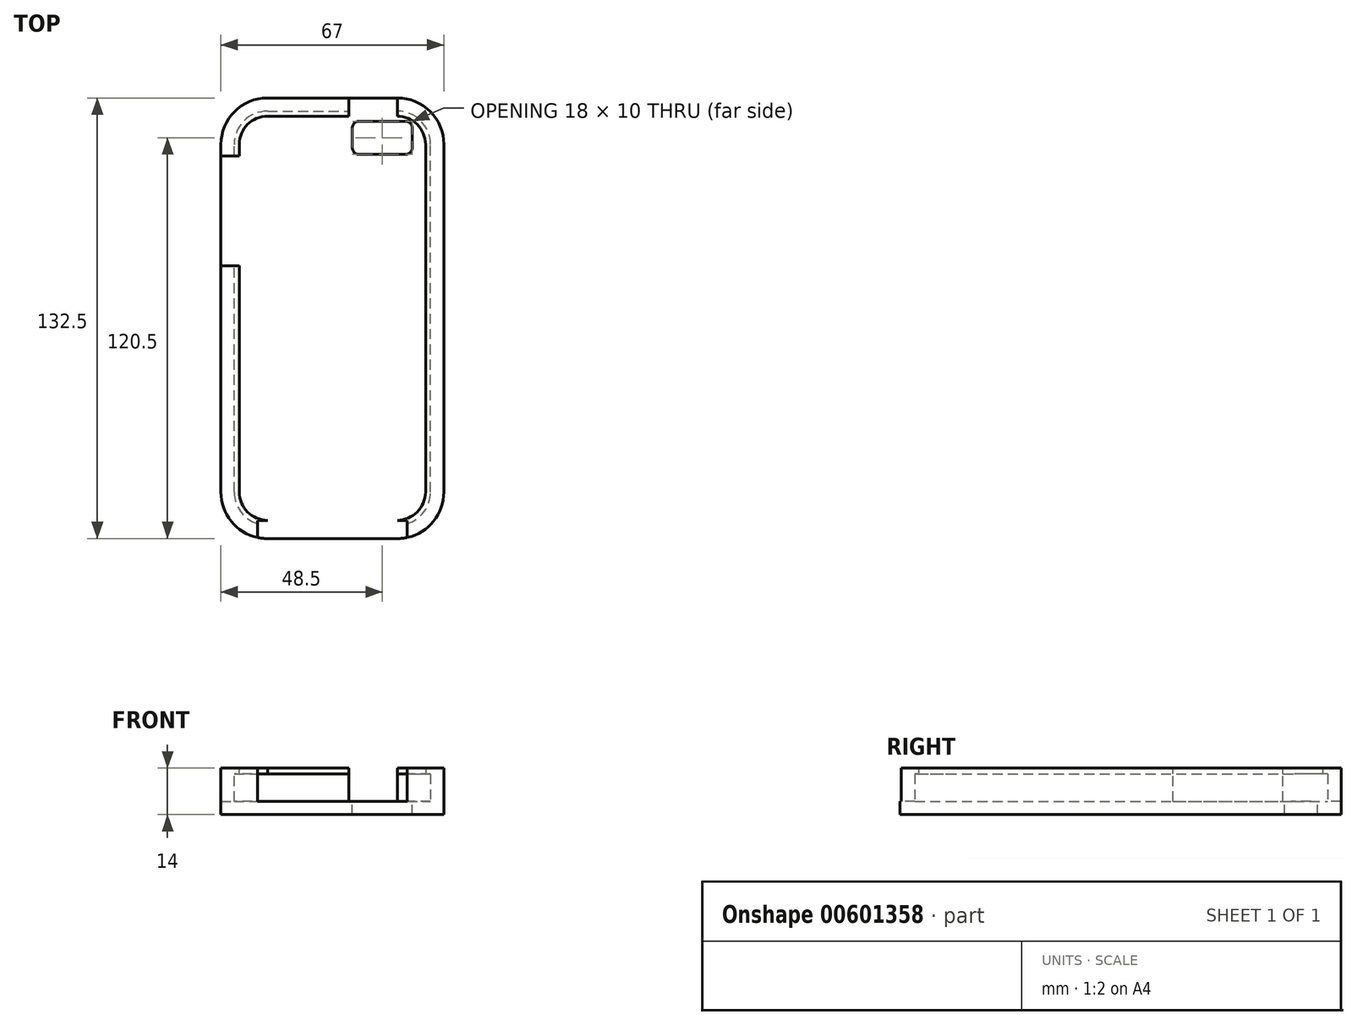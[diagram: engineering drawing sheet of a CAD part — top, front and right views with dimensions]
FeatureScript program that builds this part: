
annotation { "Feature Type Name" : "Feature", "Feature Type Description" : "" }
export const myFeature = defineFeature(function(context is Context, id is Id, definition is map)
    precondition{}
    {
        {
            var Q0;
            Q0=qCreatedBy(makeId("Top.planeOp"),FACE);
            var sketch = newSketch(context, id + "F0", { "sketchPlane" : qUnion([Q0])});
            skLineSegment(sketch, "E0.bottom", {"start": v(10, 0) * mm, "end": v(49, 0) * mm});
            skLineSegment(sketch, "E0.top", {"start": v(10, 124.5) * mm, "end": v(49, 124.5) * mm});
            skLineSegment(sketch, "E0.left", {"start": v(0, 10) * mm, "end": v(0, 114.5) * mm});
            skLineSegment(sketch, "E0.right", {"start": v(59, 10) * mm, "end": v(59, 114.5) * mm});
            skPoint(sketch, "E1.visualSharp", {"position": v(0, 124.5) * mm});
            skArc(sketch, "E1.filletArc", {"start": v(10, 124.5) * mm, "mid": v(2.93, 121.57) * mm, "end": v(0, 114.5) * mm});
            skPoint(sketch, "E2.visualSharp", {"position": v(59, 124.5) * mm});
            skArc(sketch, "E2.filletArc", {"start": v(59, 114.5) * mm, "mid": v(56.07, 121.57) * mm, "end": v(49, 124.5) * mm});
            skPoint(sketch, "E3.visualSharp", {"position": v(59, 0) * mm});
            skArc(sketch, "E3.filletArc", {"start": v(49, 0) * mm, "mid": v(56.07, 2.93) * mm, "end": v(59, 10) * mm});
            skPoint(sketch, "E4.visualSharp", {"position": v(0, 0) * mm});
            skArc(sketch, "E4.filletArc", {"start": v(0, 10) * mm, "mid": v(2.93, 2.93) * mm, "end": v(10, 0) * mm});
            skLineSegment(sketch, "E5.0", {"start": v(63, 10) * mm, "end": v(63, 114.5) * mm});
            skArc(sketch, "E5.1", {"start": v(49, -4) * mm, "mid": v(58.9, 0.1) * mm, "end": v(63, 10) * mm});
            skArc(sketch, "E5.2", {"start": v(63, 114.5) * mm, "mid": v(58.9, 124.4) * mm, "end": v(49, 128.5) * mm});
            skLineSegment(sketch, "E5.3", {"start": v(10, -4) * mm, "end": v(49, -4) * mm});
            skLineSegment(sketch, "E5.4", {"start": v(10, 128.5) * mm, "end": v(49, 128.5) * mm});
            skArc(sketch, "E5.5", {"start": v(10, 128.5) * mm, "mid": v(0.1, 124.4) * mm, "end": v(-4, 114.5) * mm});
            skLineSegment(sketch, "E5.6", {"start": v(-4, 10) * mm, "end": v(-4, 114.5) * mm});
            skArc(sketch, "E5.7", {"start": v(-4, 10) * mm, "mid": v(0.1, 0.1) * mm, "end": v(10, -4) * mm});
            skLineSegment(sketch, "E6.bottom", {"start": v(51.5, 121.5) * mm, "end": v(37.5, 121.5) * mm});
            skLineSegment(sketch, "E6.top", {"start": v(51.5, 111.5) * mm, "end": v(37.5, 111.5) * mm});
            skLineSegment(sketch, "E6.left", {"start": v(53.5, 119.5) * mm, "end": v(53.5, 113.5) * mm});
            skLineSegment(sketch, "E6.right", {"start": v(35.5, 119.5) * mm, "end": v(35.5, 113.5) * mm});
            skPoint(sketch, "E7.visualSharp", {"position": v(35.5, 121.5) * mm});
            skArc(sketch, "E7.filletArc", {"start": v(37.5, 121.5) * mm, "mid": v(36.09, 120.91) * mm, "end": v(35.5, 119.5) * mm});
            skPoint(sketch, "E8.visualSharp", {"position": v(53.5, 121.5) * mm});
            skArc(sketch, "E8.filletArc", {"start": v(53.5, 119.5) * mm, "mid": v(52.91, 120.91) * mm, "end": v(51.5, 121.5) * mm});
            skPoint(sketch, "E9.visualSharp", {"position": v(53.5, 111.5) * mm});
            skArc(sketch, "E9.filletArc", {"start": v(51.5, 111.5) * mm, "mid": v(52.91, 112.09) * mm, "end": v(53.5, 113.5) * mm});
            skPoint(sketch, "E10.visualSharp", {"position": v(35.5, 111.5) * mm});
            skArc(sketch, "E10.filletArc", {"start": v(35.5, 113.5) * mm, "mid": v(36.09, 112.09) * mm, "end": v(37.5, 111.5) * mm});
            skArc(sketch, "E11.0", {"start": v(49, 1.5) * mm, "mid": v(55.01, 3.99) * mm, "end": v(57.5, 10) * mm});
            skLineSegment(sketch, "E11.1", {"start": v(10, 1.5) * mm, "end": v(49, 1.5) * mm});
            skLineSegment(sketch, "E11.2", {"start": v(57.5, 10) * mm, "end": v(57.5, 114.5) * mm});
            skArc(sketch, "E11.3", {"start": v(1.5, 10) * mm, "mid": v(3.99, 3.99) * mm, "end": v(10, 1.5) * mm});
            skArc(sketch, "E11.4", {"start": v(57.5, 114.5) * mm, "mid": v(55.01, 120.51) * mm, "end": v(49, 123) * mm});
            skLineSegment(sketch, "E11.5", {"start": v(10, 123) * mm, "end": v(49, 123) * mm});
            skArc(sketch, "E11.6", {"start": v(10, 123) * mm, "mid": v(3.99, 120.51) * mm, "end": v(1.5, 114.5) * mm});
            skLineSegment(sketch, "E11.7", {"start": v(1.5, 10) * mm, "end": v(1.5, 114.5) * mm});
            skSolve(sketch);
        }
        {
            var Q0;
            Q0=makeQuery(id+"F0.imprint","IMPRINT",FACE,{"disambiguationData":[TD([[makeQuery(id+"F0.imprint","IMPRINT",EDGE,{"derivedFrom":sQuery(id+"F0.wireOp",EDGE,"E6.bottom")}),-1.0]])]});
            var Q1;
            Q1=makeQuery(id+"F0.imprint","IMPRINT",FACE,{"disambiguationData":[TD([[makeQuery(id+"F0.imprint","IMPRINT",EDGE,{"derivedFrom":sQuery(id+"F0.wireOp",EDGE,"E0.bottom")}),-1.0]])]});
            var Q2;
            Q2=makeQuery(id+"F0.imprint","IMPRINT",FACE,{"disambiguationData":[TD([[makeQuery(id+"F0.imprint","IMPRINT",EDGE,{"derivedFrom":sQuery(id+"F0.wireOp",EDGE,"E0.bottom")}),1.0]])]});
            extrude(context, id + "F1", {"entities" : qUnion([Q0, Q1, Q2]), "oppositeDirection" : true, "depth" : 4 * mm, "offsetDistance" : 25 * mm});
        }
        {
            var Q0;
            Q0=makeQuery(id+"F0.imprint","IMPRINT",FACE,{"disambiguationData":[TD([[makeQuery(id+"F0.imprint","IMPRINT",EDGE,{"derivedFrom":sQuery(id+"F0.wireOp",EDGE,"E0.bottom")}),1.0]])]});
            var Q1;
            Q1=makeQuery(id+"F0.imprint","IMPRINT",FACE,{"disambiguationData":[TD([[makeQuery(id+"F0.imprint","IMPRINT",EDGE,{"derivedFrom":sQuery(id+"F0.wireOp",EDGE,"E0.bottom")}),-1.0]])]});
            extrude(context, id + "F2", {"entities" : qUnion([Q0, Q1]), "operationType" : NewBodyOperationType.ADD, "depth" : 10 * mm, "offsetDistance" : 25 * mm});
        }
        {
            var Q0;
            Q0=makeQuery(id+"F0.imprint","IMPRINT",FACE,{"disambiguationData":[TD([[makeQuery(id+"F0.imprint","IMPRINT",EDGE,{"derivedFrom":sQuery(id+"F0.wireOp",EDGE,"E0.bottom")}),1.0]])]});
            extrude(context, id + "F3", {"entities" : qUnion([Q0]), "operationType" : NewBodyOperationType.REMOVE, "depth" : 8.2 * mm, "offsetDistance" : 25 * mm});
        }
        {
            var Q0;
            Q0=makeQuery(id+"F2.opExtrude","CAP_FACE",FACE,{"disambiguationData":[OSD([sQuery(id+"F0.wireOp",EDGE,"E5.0"),sQuery(id+"F0.wireOp",EDGE,"E5.1"),sQuery(id+"F0.wireOp",EDGE,"E5.2"),sQuery(id+"F0.wireOp",EDGE,"E5.3"),sQuery(id+"F0.wireOp",EDGE,"E5.4"),sQuery(id+"F0.wireOp",EDGE,"E5.5"),sQuery(id+"F0.wireOp",EDGE,"E5.6"),sQuery(id+"F0.wireOp",EDGE,"E5.7"),sQuery(id+"F0.wireOp",EDGE,"E11.0"),sQuery(id+"F0.wireOp",EDGE,"E11.1"),sQuery(id+"F0.wireOp",EDGE,"E11.2"),sQuery(id+"F0.wireOp",EDGE,"E11.3"),sQuery(id+"F0.wireOp",EDGE,"E11.4"),sQuery(id+"F0.wireOp",EDGE,"E11.5"),sQuery(id+"F0.wireOp",EDGE,"E11.6"),sQuery(id+"F0.wireOp",EDGE,"E11.7")])],"isStart":false});
            var sketch = newSketch(context, id + "F4", { "sketchPlane" : qUnion([Q0])});
            skLineSegment(sketch, "E12.bottom", {"start": v(-4, 111) * mm, "end": v(1.5, 111) * mm});
            skLineSegment(sketch, "E12.top", {"start": v(-4, 78) * mm, "end": v(1.5, 78) * mm});
            skLineSegment(sketch, "E12.left", {"start": v(-4, 111) * mm, "end": v(-4, 78) * mm});
            skLineSegment(sketch, "E12.right", {"start": v(1.5, 111) * mm, "end": v(1.5, 78) * mm});
            skLineSegment(sketch, "E13", {"start": v(29.5, 1.5) * mm, "end": v(29.5, -4) * mm, "construction": true});
            skLineSegment(sketch, "E14.bottom", {"start": v(52, 1.5) * mm, "end": v(7, 1.5) * mm});
            skLineSegment(sketch, "E14.top", {"start": v(52, -4) * mm, "end": v(7, -4) * mm});
            skLineSegment(sketch, "E14.left", {"start": v(52, 1.5) * mm, "end": v(52, -4) * mm});
            skLineSegment(sketch, "E14.right", {"start": v(7, 1.5) * mm, "end": v(7, -4) * mm});
            skPoint(sketch, "E14.middle", {"position": v(29.5, -1.25) * mm});
            skLineSegment(sketch, "E15.bottom", {"start": v(34.5, 128.5) * mm, "end": v(49, 128.5) * mm});
            skLineSegment(sketch, "E15.top", {"start": v(34.5, 123) * mm, "end": v(49, 123) * mm});
            skLineSegment(sketch, "E15.left", {"start": v(34.5, 128.5) * mm, "end": v(34.5, 123) * mm});
            skLineSegment(sketch, "E15.right", {"start": v(49, 128.5) * mm, "end": v(49, 123) * mm});
            skSolve(sketch);
        }
        {
            var Q0;
            Q0=makeQuery(id+"F4.imprint","IMPRINT",FACE,{"disambiguationData":[TD([[makeQuery(id+"F4.imprint","IMPRINT",EDGE,{"derivedFrom":sQuery(id+"F4.wireOp",EDGE,"E12.bottom")}),-1.0]])]});
            var Q1;
            Q1=makeQuery(id+"F4.imprint","IMPRINT",FACE,{"disambiguationData":[TD([[makeQuery(id+"F4.imprint","IMPRINT",EDGE,{"derivedFrom":sQuery(id+"F4.wireOp",EDGE,"E15.bottom")}),-1.0]])]});
            var Q2;
            {var subQ5=sQuery(id+"F4.wireOp",EDGE,"E14.bottom");var subQ9=makeQuery(id+"F4.imprint","INTERSECT",VERTEX,{"derivedFrom":[makeQuery(id+"F2.opExtrude","CAP_EDGE",EDGE,{"disambiguationData":[OSD([sQuery(id+"F0.wireOp",EDGE,"E11.0")])],"isStart":false}),subQ5]});var subQ10=sQuery(id+"F4.wireOp",EDGE,"E14.left");var subQ11=makeQuery(id+"F4.imprint","INTERSECT",VERTEX,{"derivedFrom":[subQ5,subQ10]});Q2=makeQuery(id+"F4.imprint","IMPRINT",FACE,{"disambiguationData":[TD([[makeQuery(id+"F4.imprint","IMPRINT",EDGE,{"disambiguationData":[TD([[subQ9,1.0],[subQ11,-1.0]])],"derivedFrom":subQ5}),1.0]])]});}
            extrude(context, id + "F5", {"entities" : qUnion([Q0, Q1, Q2]), "operationType" : NewBodyOperationType.REMOVE, "oppositeDirection" : true, "depth" : 10 * mm, "offsetDistance" : 25 * mm});
        }
    });
